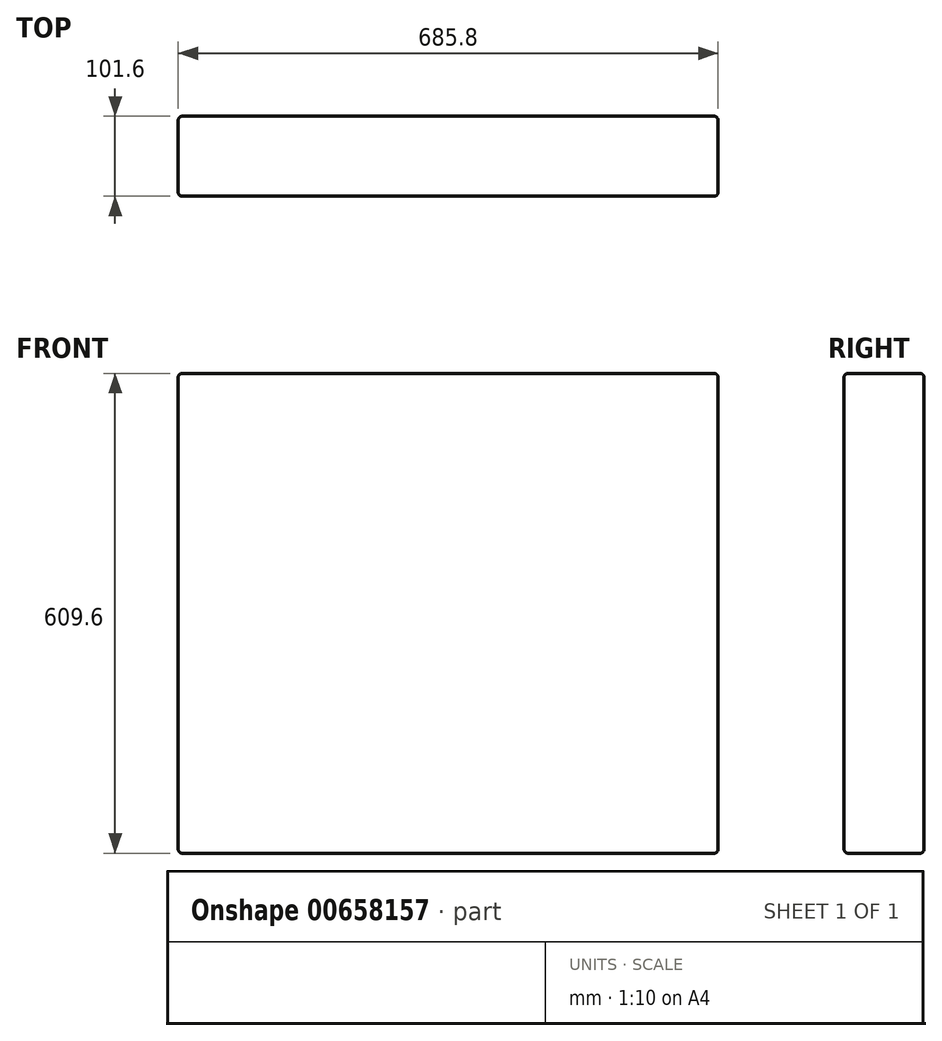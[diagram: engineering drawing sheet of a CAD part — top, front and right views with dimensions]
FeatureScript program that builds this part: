
annotation { "Feature Type Name" : "Feature", "Feature Type Description" : "" }
export const myFeature = defineFeature(function(context is Context, id is Id, definition is map)
    precondition{}
    {
        {
            var Q0;
            Q0=qCreatedBy(makeId("Front.planeOp"),FACE);
            var sketch = newSketch(context, id + "F0", { "sketchPlane" : qUnion([Q0])});
            skLineSegment(sketch, "E0.bottom", {"start": v(0, 0) * mm, "end": v(685.8, 0) * mm});
            skLineSegment(sketch, "E0.top", {"start": v(0, 609.6) * mm, "end": v(685.8, 609.6) * mm});
            skLineSegment(sketch, "E0.left", {"start": v(0, 0) * mm, "end": v(0, 609.6) * mm});
            skLineSegment(sketch, "E0.right", {"start": v(685.8, 0) * mm, "end": v(685.8, 609.6) * mm});
            skSolve(sketch);
        }
        {
            var Q0;
            Q0=makeQuery(id+"F0.imprint","IMPRINT",FACE,{"disambiguationData":[TD([[makeQuery(id+"F0.imprint","IMPRINT",EDGE,{"derivedFrom":sQuery(id+"F0.wireOp",EDGE,"E0.bottom")}),1.0]])]});
            extrude(context, id + "F1", {"entities" : qUnion([Q0]), "oppositeDirection" : true, "depth" : 101.6 * mm, "offsetDistance" : 25.4 * mm});
        }
        {
            var Q0;
            Q0=makeQuery(id+"F1.opExtrude","CAP_EDGE",EDGE,{"disambiguationData":[OSD([sQuery(id+"F0.wireOp",EDGE,"E0.right")])],"isStart":true});
            var Q1;
            Q1=makeQuery(id+"F1.opExtrude","CAP_EDGE",EDGE,{"disambiguationData":[OSD([sQuery(id+"F0.wireOp",EDGE,"E0.right")])],"isStart":false});
            var Q2;
            Q2=makeQuery(id+"F1.opExtrude","CAP_EDGE",EDGE,{"disambiguationData":[OSD([sQuery(id+"F0.wireOp",EDGE,"E0.top")])],"isStart":true});
            var Q3;
            Q3=makeQuery(id+"F1.opExtrude","SWEPT_EDGE",EDGE,{"disambiguationData":[OSD([sQuery(id+"F0.wireOp",EDGE,"E0.top"),sQuery(id+"F0.wireOp",EDGE,"E0.right")])]});
            var Q4;
            Q4=makeQuery(id+"F1.opExtrude","CAP_EDGE",EDGE,{"disambiguationData":[OSD([sQuery(id+"F0.wireOp",EDGE,"E0.top")])],"isStart":false});
            var Q5;
            Q5=makeQuery(id+"F1.opExtrude","CAP_EDGE",EDGE,{"disambiguationData":[OSD([sQuery(id+"F0.wireOp",EDGE,"E0.bottom")])],"isStart":true});
            var Q6;
            Q6=makeQuery(id+"F1.opExtrude","CAP_EDGE",EDGE,{"disambiguationData":[OSD([sQuery(id+"F0.wireOp",EDGE,"E0.left")])],"isStart":true});
            var Q7;
            Q7=makeQuery(id+"F1.opExtrude","CAP_EDGE",EDGE,{"disambiguationData":[OSD([sQuery(id+"F0.wireOp",EDGE,"E0.bottom")])],"isStart":false});
            var Q8;
            Q8=makeQuery(id+"F1.opExtrude","CAP_FACE",FACE,{"disambiguationData":[OSD([sQuery(id+"F0.wireOp",EDGE,"E0.bottom"),sQuery(id+"F0.wireOp",EDGE,"E0.top"),sQuery(id+"F0.wireOp",EDGE,"E0.left"),sQuery(id+"F0.wireOp",EDGE,"E0.right")])],"isStart":false});
            var Q9;
            Q9=makeQuery(id+"F1.opExtrude","SWEPT_EDGE",EDGE,{"disambiguationData":[OSD([sQuery(id+"F0.wireOp",EDGE,"E0.bottom"),sQuery(id+"F0.wireOp",EDGE,"E0.right")])]});
            var Q10;
            Q10=makeQuery(id+"F1.opExtrude","SWEPT_EDGE",EDGE,{"disambiguationData":[OSD([sQuery(id+"F0.wireOp",EDGE,"E0.bottom"),sQuery(id+"F0.wireOp",EDGE,"E0.left")])]});
            var Q11;
            Q11=makeQuery(id+"F1.opExtrude","SWEPT_EDGE",EDGE,{"disambiguationData":[OSD([sQuery(id+"F0.wireOp",EDGE,"E0.top"),sQuery(id+"F0.wireOp",EDGE,"E0.left")])]});
            fillet(context, id + "F2", {"entities" : qUnion([Q0, Q1, Q2, Q3, Q4, Q5, Q6, Q7, Q8, Q9, Q10, Q11]), "radius" : 5.08 * mm, "tangentPropagation" : true, "allowEdgeOverflow" : false});
        }
    });
